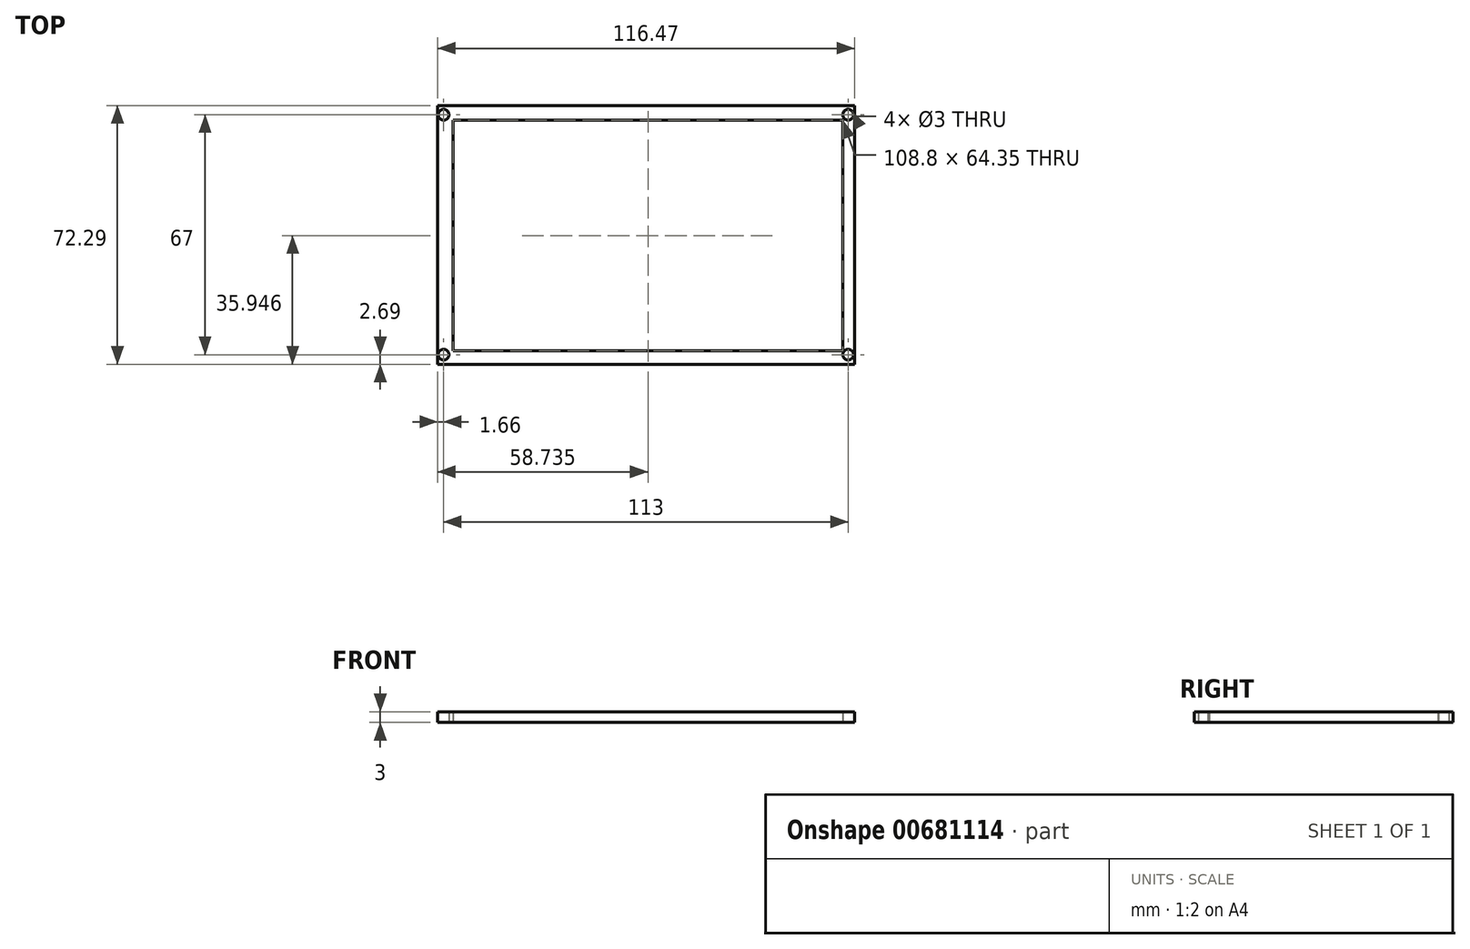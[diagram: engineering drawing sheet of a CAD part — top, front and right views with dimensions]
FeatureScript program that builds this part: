
annotation { "Feature Type Name" : "Feature", "Feature Type Description" : "" }
export const myFeature = defineFeature(function(context is Context, id is Id, definition is map)
    precondition{}
    {
        {
            var Q0;
            Q0=qCreatedBy(makeId("Top.planeOp"),FACE);
            var sketch = newSketch(context, id + "F0", { "sketchPlane" : qUnion([Q0])});
            skLineSegment(sketch, "E0.bottom", {"start": v(-70.5, 47.5) * mm, "end": v(70.5, 47.5) * mm});
            skLineSegment(sketch, "E0.top", {"start": v(-70.5, -47.5) * mm, "end": v(70.5, -47.5) * mm});
            skLineSegment(sketch, "E0.left", {"start": v(-70.5, 47.5) * mm, "end": v(-70.5, -47.5) * mm});
            skLineSegment(sketch, "E0.right", {"start": v(70.5, 47.5) * mm, "end": v(70.5, -47.5) * mm});
            skPoint(sketch, "E0.middle", {"position": v(0, 0) * mm});
            skLineSegment(sketch, "E1.bottom", {"start": v(-56.5, 33.5) * mm, "end": v(56.5, 33.5) * mm, "construction": true});
            skLineSegment(sketch, "E1.top", {"start": v(-56.5, -33.5) * mm, "end": v(56.5, -33.5) * mm, "construction": true});
            skLineSegment(sketch, "E1.left", {"start": v(-56.5, 33.5) * mm, "end": v(-56.5, -33.5) * mm, "construction": true});
            skLineSegment(sketch, "E1.right", {"start": v(56.5, 33.5) * mm, "end": v(56.5, -33.5) * mm, "construction": true});
            skCircle(sketch, "E2", {"center": v(-56.5, 33.5) * mm, "radius": 1.5 * mm});
            skCircle(sketch, "E3", {"center": v(-56.5, -33.5) * mm, "radius": 1.5 * mm});
            skCircle(sketch, "E4", {"center": v(56.5, -33.5) * mm, "radius": 1.5 * mm});
            skCircle(sketch, "E5", {"center": v(56.5, 33.5) * mm, "radius": 1.5 * mm});
            skLineSegment(sketch, "E6.bottom", {"start": v(37.5, -30) * mm, "end": v(-37.5, -30) * mm});
            skLineSegment(sketch, "E6.top", {"start": v(37.5, 30) * mm, "end": v(-37.5, 30) * mm});
            skLineSegment(sketch, "E6.left", {"start": v(37.5, -30) * mm, "end": v(37.5, 30) * mm});
            skLineSegment(sketch, "E6.right", {"start": v(-37.5, -30) * mm, "end": v(-37.5, 30) * mm});
            skLineSegment(sketch, "E7.bottom", {"start": v(-58.16, 36.1) * mm, "end": v(58.3, 36.1) * mm});
            skLineSegment(sketch, "E7.top", {"start": v(-58.16, -36.2) * mm, "end": v(58.3, -36.2) * mm});
            skLineSegment(sketch, "E7.left", {"start": v(-58.16, 36.1) * mm, "end": v(-58.16, -36.2) * mm});
            skLineSegment(sketch, "E7.right", {"start": v(58.3, 36.1) * mm, "end": v(58.3, -36.2) * mm});
            skLineSegment(sketch, "E8.bottom", {"start": v(-53.82, 31.93) * mm, "end": v(54.97, 31.93) * mm});
            skLineSegment(sketch, "E8.top", {"start": v(-53.82, -32.42) * mm, "end": v(54.97, -32.42) * mm});
            skLineSegment(sketch, "E8.left", {"start": v(-53.82, 31.93) * mm, "end": v(-53.82, -32.42) * mm});
            skLineSegment(sketch, "E8.right", {"start": v(54.97, 31.93) * mm, "end": v(54.97, -32.42) * mm});
            skSolve(sketch);
        }
        {
            var Q0;
            Q0=makeQuery(id+"F0.imprint","IMPRINT",FACE,{"disambiguationData":[TD([[makeQuery(id+"F0.imprint","IMPRINT",EDGE,{"derivedFrom":sQuery(id+"F0.wireOp",EDGE,"E2")}),-1.0]])]});
            extrude(context, id + "F1", {"entities" : qUnion([Q0]), "depth" : 3 * mm, "offsetDistance" : 25 * mm});
        }
    });
